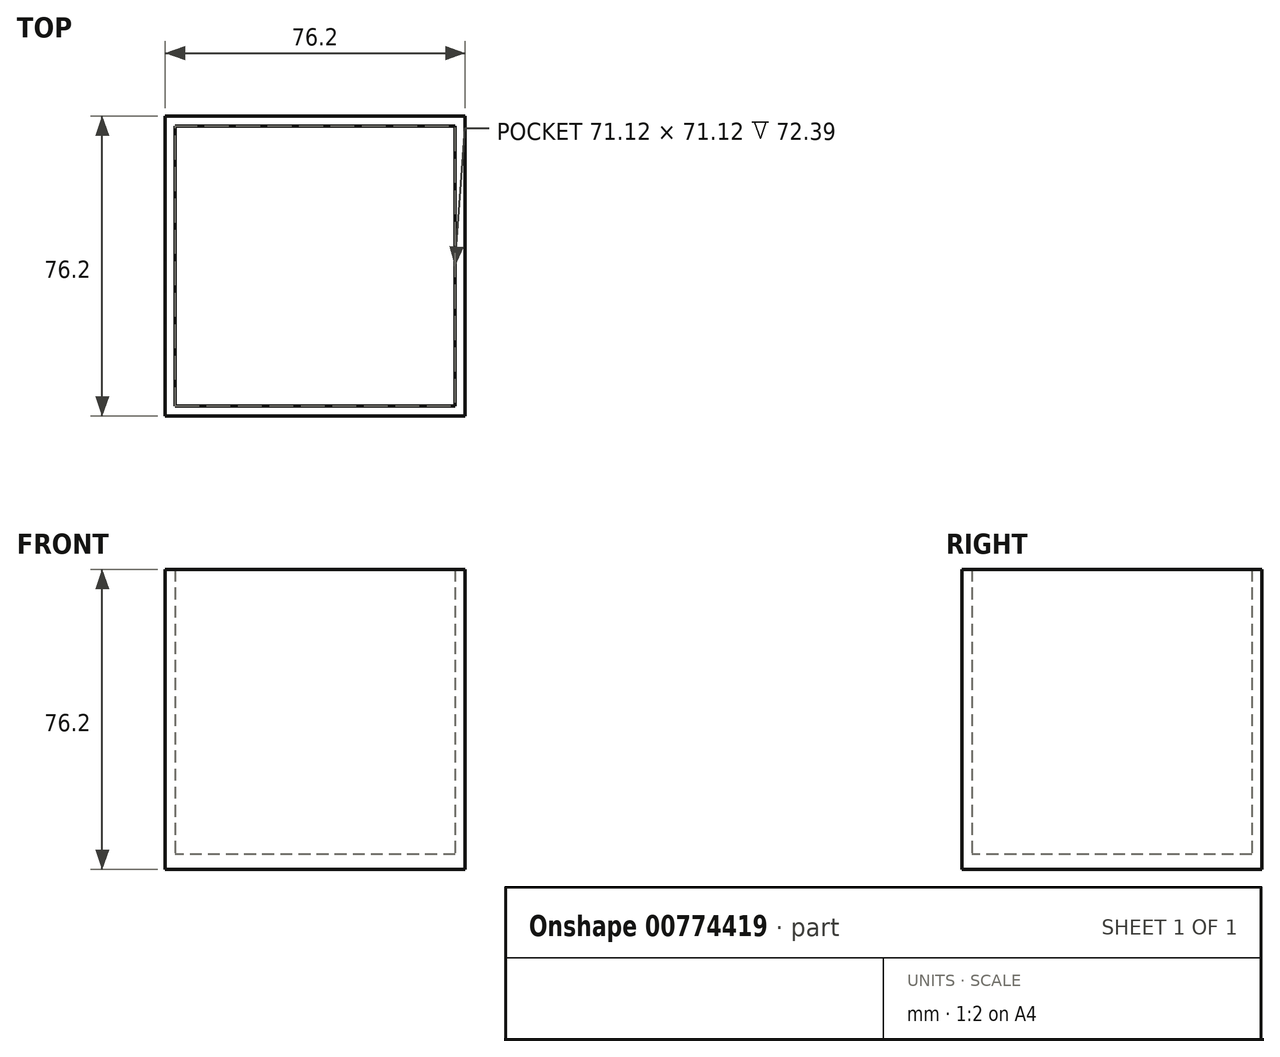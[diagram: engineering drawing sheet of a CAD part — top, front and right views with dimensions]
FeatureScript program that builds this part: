
annotation { "Feature Type Name" : "Feature", "Feature Type Description" : "" }
export const myFeature = defineFeature(function(context is Context, id is Id, definition is map)
    precondition{}
    {
        {
            var Q0;
            Q0=qCreatedBy(makeId("Top.planeOp"),FACE);
            var sketch = newSketch(context, id + "F0", { "sketchPlane" : qUnion([Q0])});
            skLineSegment(sketch, "E0.bottom", {"start": v(38.1, 38.1) * mm, "end": v(-38.1, 38.1) * mm});
            skLineSegment(sketch, "E0.top", {"start": v(38.1, -38.1) * mm, "end": v(-38.1, -38.1) * mm});
            skLineSegment(sketch, "E0.left", {"start": v(38.1, 38.1) * mm, "end": v(38.1, -38.1) * mm});
            skLineSegment(sketch, "E0.right", {"start": v(-38.1, 38.1) * mm, "end": v(-38.1, -38.1) * mm});
            skPoint(sketch, "E0.middle", {"position": v(0, 0) * mm});
            skSolve(sketch);
        }
        {
            var Q0;
            Q0=qSketchRegion(id+"F0",true);
            extrude(context, id + "F1", {"entities" : qUnion([Q0]), "depth" : 3.8 * mm, "offsetDistance" : 25.4 * mm});
        }
        {
            var Q0;
            Q0=makeQuery(id+"F1.opExtrude","CAP_FACE",FACE,{"disambiguationData":[OSD([sQuery(id+"F0.wireOp",EDGE,"E0.bottom"),sQuery(id+"F0.wireOp",EDGE,"E0.top"),sQuery(id+"F0.wireOp",EDGE,"E0.left"),sQuery(id+"F0.wireOp",EDGE,"E0.right")])],"isStart":false});
            var sketch = newSketch(context, id + "F2", { "sketchPlane" : qUnion([Q0])});
            skLineSegment(sketch, "E1.bottom", {"start": v(35.56, 35.56) * mm, "end": v(-35.56, 35.56) * mm});
            skLineSegment(sketch, "E1.top", {"start": v(35.56, -35.56) * mm, "end": v(-35.56, -35.56) * mm});
            skLineSegment(sketch, "E1.left", {"start": v(35.56, 35.56) * mm, "end": v(35.56, -35.56) * mm});
            skLineSegment(sketch, "E1.right", {"start": v(-35.56, 35.56) * mm, "end": v(-35.56, -35.56) * mm});
            skPoint(sketch, "E1.middle", {"position": v(0, 0) * mm});
            skLineSegment(sketch, "E2.bottom", {"start": v(38.1, 38.1) * mm, "end": v(-38.1, 38.1) * mm});
            skLineSegment(sketch, "E2.top", {"start": v(38.1, -38.1) * mm, "end": v(-38.1, -38.1) * mm});
            skLineSegment(sketch, "E2.left", {"start": v(38.1, 38.1) * mm, "end": v(38.1, -38.1) * mm});
            skLineSegment(sketch, "E2.right", {"start": v(-38.1, 38.1) * mm, "end": v(-38.1, -38.1) * mm});
            skSolve(sketch);
        }
        {
            var Q0;
            Q0=qSketchRegion(id+"F2",true);
            extrude(context, id + "F3", {"entities" : qUnion([Q0]), "operationType" : NewBodyOperationType.ADD, "depth" : 72.39 * mm, "offsetDistance" : 25.4 * mm});
        }
    });
